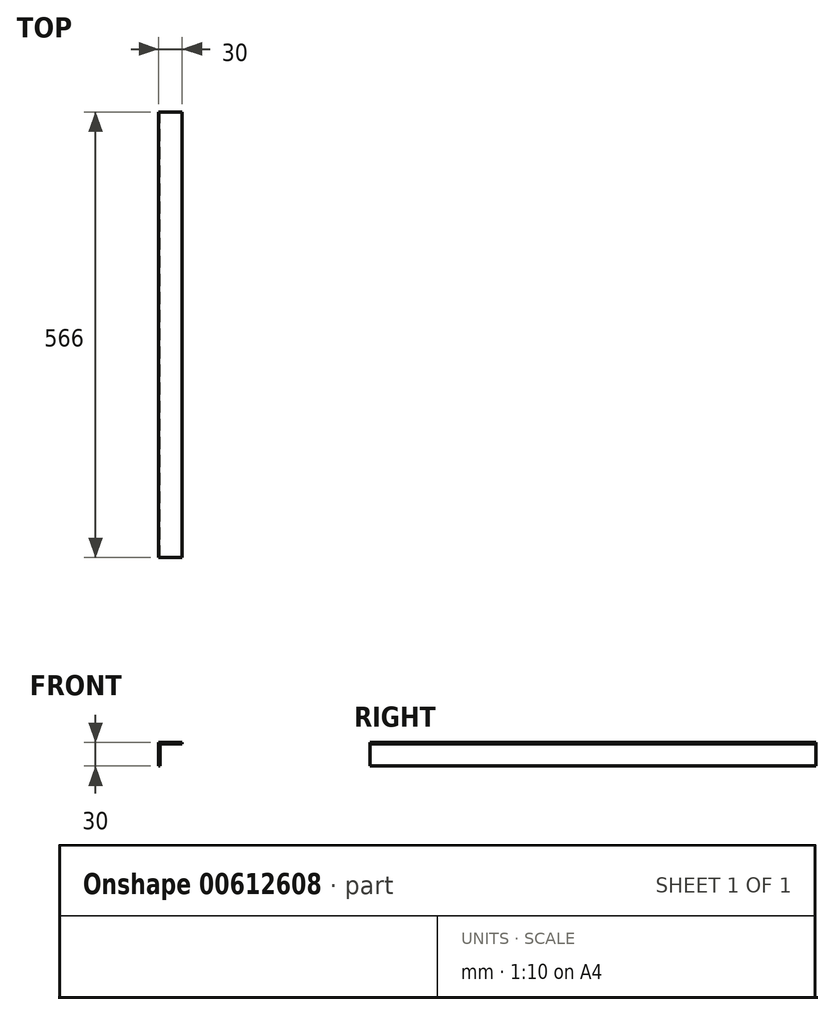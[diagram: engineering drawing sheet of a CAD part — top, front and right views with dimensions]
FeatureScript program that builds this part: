
annotation { "Feature Type Name" : "Feature", "Feature Type Description" : "" }
export const myFeature = defineFeature(function(context is Context, id is Id, definition is map)
    precondition{}
    {
        {
            var Q0;
            Q0=qCreatedBy(makeId("Front.planeOp"),FACE);
            var sketch = newSketch(context, id + "F0", { "sketchPlane" : qUnion([Q0])});
            skLineSegment(sketch, "E0", {"start": v(0, 0) * mm, "end": v(0, 30) * mm});
            skLineSegment(sketch, "E1", {"start": v(0, 30) * mm, "end": v(30, 30) * mm});
            skLineSegment(sketch, "E2.0", {"start": v(2, 28) * mm, "end": v(30, 28) * mm});
            skLineSegment(sketch, "E2.1", {"start": v(2, 0) * mm, "end": v(2, 28) * mm});
            skLineSegment(sketch, "E3", {"start": v(30, 30) * mm, "end": v(30, 28) * mm});
            skLineSegment(sketch, "E4", {"start": v(0, 0) * mm, "end": v(2, 0) * mm});
            skSolve(sketch);
        }
        {
            var Q0;
            Q0=makeQuery(id+"F0.imprint","IMPRINT",FACE,{"disambiguationData":[TD([[makeQuery(id+"F0.imprint","IMPRINT",EDGE,{"derivedFrom":sQuery(id+"F0.wireOp",EDGE,"E0")}),-1.0]])]});
            extrude(context, id + "F1", {"entities" : qUnion([Q0]), "depth" : 646 * mm - 80 * mm, "offsetDistance" : 25.4 * mm});
        }
    });
